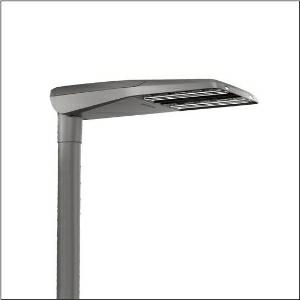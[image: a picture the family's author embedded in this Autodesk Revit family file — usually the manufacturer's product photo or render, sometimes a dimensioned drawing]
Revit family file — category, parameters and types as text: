
# Revit family: streetlight_sl_11_iq_midi___st1_2a_5xc3a41e08me_8609
name_source: partatom
category: Lighting Fixtures
units: mm (PartAtom-declared; Revit-internal decimal feet)

## family parameters
Cut with Voids When Loaded = No
Host = Face
Light Source = No
Part Type = Normal
Room Calculation Point = No
Round Connector Dimension = Use Diameter
Shared = No

## types (1)
- --- (1 x LED, 18900 lm, 124.7 W, 4000K)
    Apparent Load = 125 VA
    CIE Flux Codes = 32 70 96 100 100
    Color Rendering = 70
    Color Temperature = 4000K
    Default Elevation = 1800 mm
    Description = Streetlight SL 11 iQ midi, mast luminaire, primary light control with 3 zone facetted reflector, of plastic, silver coated, highly specular, primary optical cover: cover, of PMMA, transparent, light distribution: ST1.2a, light emission: direct distribution, primary light characteristic: asymmetric, installation type: post-top, side-entry, lamps: LED, High Power LED, rated values: 18.900lm | 124,7W | 151,6lm/W (begin service life); end service life: 18.900lm | 132,2W; at 50% lumin. flux: 9.450lm | 57,4W | 164,6lm/W, colour temperature: 4000K, colour rendering: CRI > 70, light colour: 740, light setting 1 begin service life: 100% | 18.900lm | 124,7W | 151,6lm/W | 4.000K, light setting 1 end service life: 132,2W, further light settings possible, control: optimised constant luminous flux control (CLO 2.0), Desk-Remote (wireless, voltage-free reading and setting of iQ features in the workshop via application-optimized NFC function/RFID function), Light-Fading, Smart-Wire, Night-Set, Lumen-Switch, Temp-Guard, Auto-Match, with cable H07RN-F 3x 1.5mm², mains connection: 230..240V, AC, 50/60Hz, connection cable pre-assembled, cable length: 12,5m, luminaire housing, of diecast aluminium, powder-coated, SITECO metallic grey (DB 702S), please order mast flange separately, inclination adjustable without tools: 0°, 5°, 10°, 15° (post-top) | 0°, -5°, -10°, -15° (side-entry), sealing non-destructively replaceable, multi-level sealing system, length: 780mm, width: 376mm, height: 118mm, mast flange for spigot size: 42mm (side-entry): 5XC10008XM4, 60/48mm (side-entry/post-top): 5XC10108XM2, 76/60mm (side-entry/post-top): 5XC10108XM1, equipment: Power, protection rating (complete): IP66, insulation class (complete): insulation class II (safety insulation), certification: CE, ENEC, ENEC+, VDE, impact resistance: IK10, permissible operating ambient temperature for outdoor applications: -25..+50°C, standard-compliant lighting for roads and squares, Environmental Product Declaration (EPD) tested and certified by an independent institute, packaging unit: 1 piece

Light Distribution: ST1.2a
    Height = 118 mm
    Lamp = 1 x LED
    Lamp Light Flux = 18900 lm
    Lamp Power = 124.7 W
    Lamp count = 1
    Length = 780 mm
    Luminous efficacy = 152 lm/W
    Manufacturer = Siteco
    ModVariant = No
    Model = 5XC3A41E08ME
    Number of Poles = 1
    OnlyDefault = Yes
    Power Factor = 1
    Product Name = Streetlight SL 11 iQ midi | ST1.2a
    Product group = mast luminaire | pylon top
    ProductGroupID = 6100
    Protection Class = Protection class II
    Protection Degree = IP 66
    RLX_Detail_Level = 1
    RLX_Emergency_Light_Flux = 0 lm
    RLX_Emergency_Type = 0
    RLX_Emergency_Type_DB = No
    RlxData = <blob elided: 71017 chars, md5=e2c52c0d>
    Socket = socket
    Standby Power = 0 W
    System Light Flux = 18900 lm
    System Power = 125 W
    Type Comments = factory setting: luminous flux: 100 % | dim-lin: 254 | 557 mA
    Type Image = l_1005960.jpg
    URL = http://relux.com
    VarID = @adj_193801
    Voltage = 0 V
    Weight = 0.00 kg
    Width = 376 mm

## geometry (parser evidence)
native form markers: Blend x4, Sweep x10
no freeform markers — native parametric forms only
